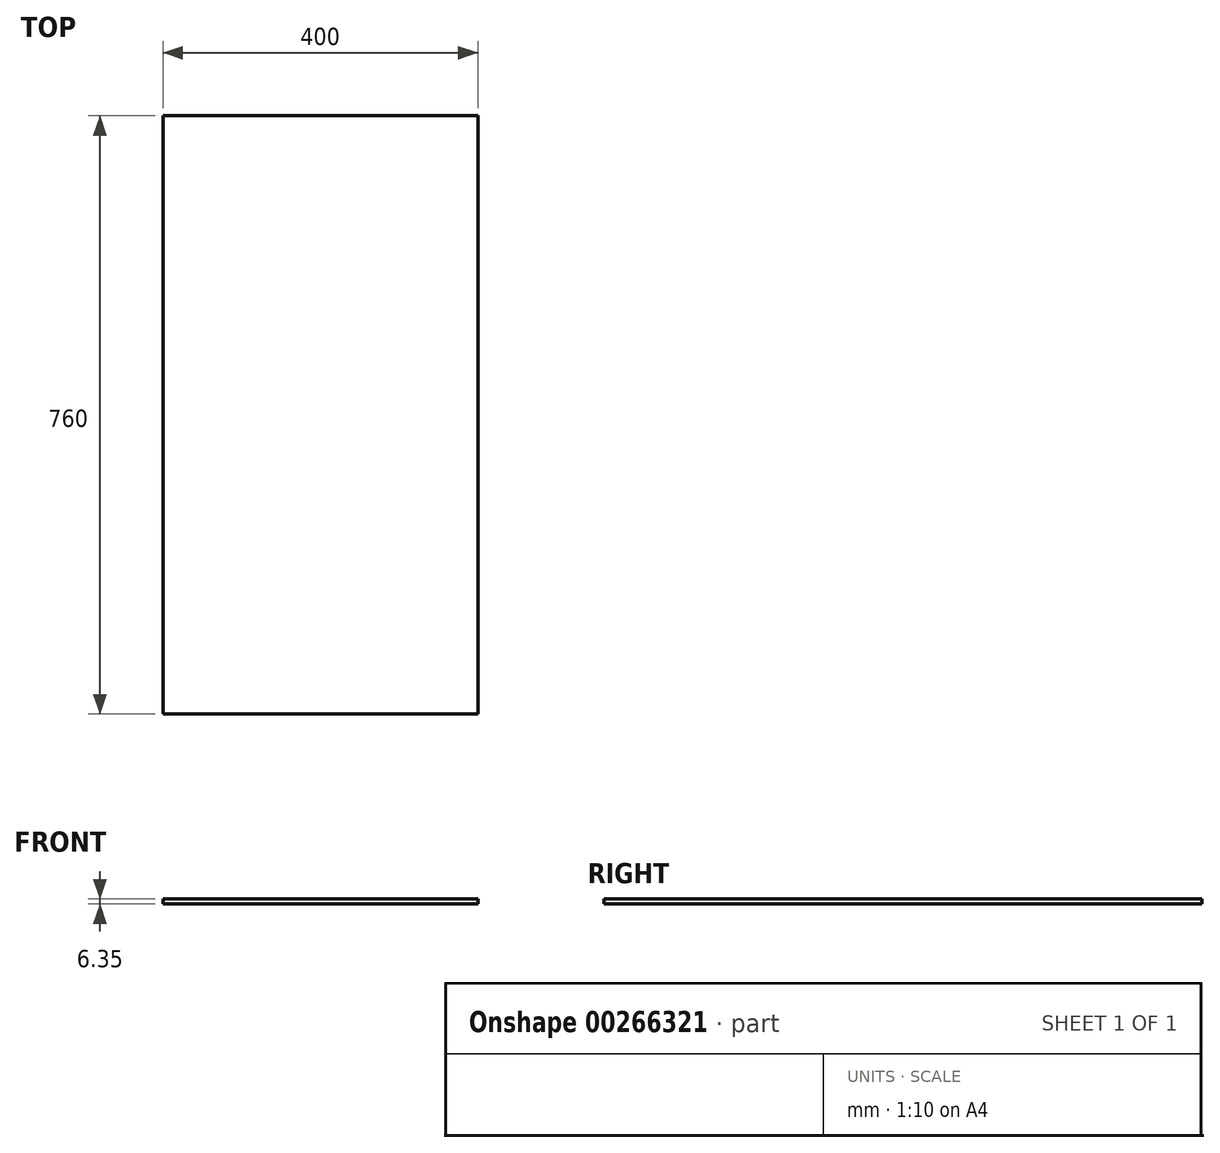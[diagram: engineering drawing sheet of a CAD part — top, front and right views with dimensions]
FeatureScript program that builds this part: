
annotation { "Feature Type Name" : "Feature", "Feature Type Description" : "" }
export const myFeature = defineFeature(function(context is Context, id is Id, definition is map)
    precondition{}
    {
        {
            var Q0;
            Q0=qCreatedBy(makeId("Top.planeOp"),FACE);
            var sketch = newSketch(context, id + "F0", { "sketchPlane" : qUnion([Q0])});
            skLineSegment(sketch, "E0.bottom", {"start": v(200, -380) * mm, "end": v(-200, -380) * mm});
            skLineSegment(sketch, "E0.top", {"start": v(200, 380) * mm, "end": v(-200, 380) * mm});
            skLineSegment(sketch, "E0.left", {"start": v(200, -380) * mm, "end": v(200, 380) * mm});
            skLineSegment(sketch, "E0.right", {"start": v(-200, -380) * mm, "end": v(-200, 380) * mm});
            skPoint(sketch, "E0.middle", {"position": v(0, 0) * mm});
            skSolve(sketch);
        }
        {
            var Q0;
            Q0=makeQuery(id+"F0.imprint","IMPRINT",FACE,{"disambiguationData":[TD([[makeQuery(id+"F0.imprint","IMPRINT",EDGE,{"derivedFrom":sQuery(id+"F0.wireOp",EDGE,"E0.bottom")}),-1.0]])]});
            extrude(context, id + "F1", {"entities" : qUnion([Q0]), "depth" : 6.35 * mm});
        }
    });
